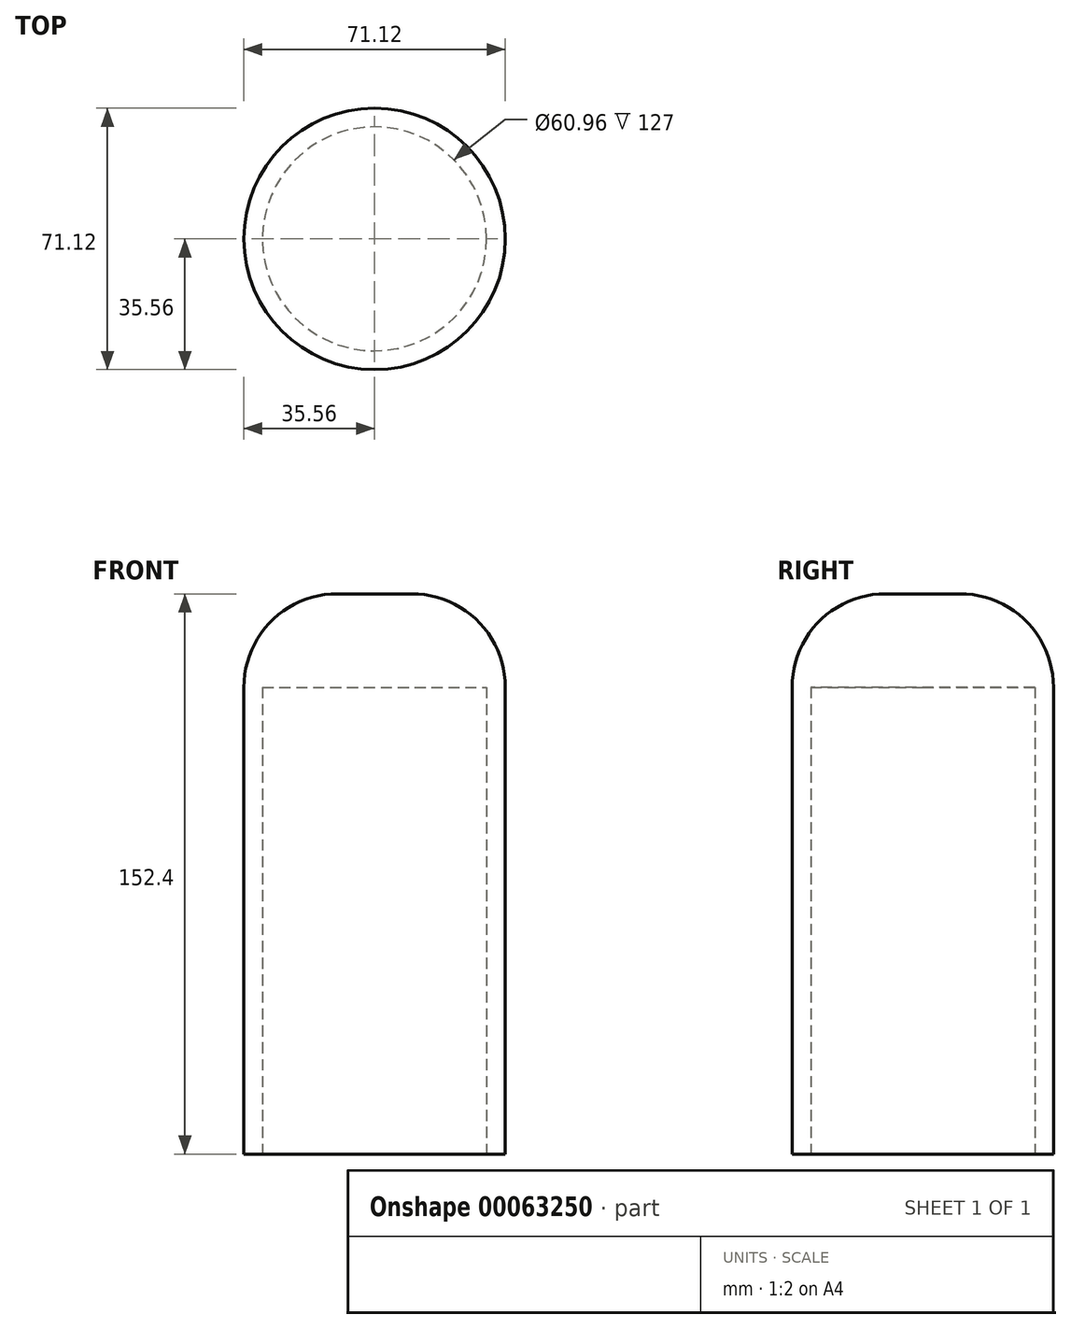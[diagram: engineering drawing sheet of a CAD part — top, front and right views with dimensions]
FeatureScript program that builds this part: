
annotation { "Feature Type Name" : "Feature", "Feature Type Description" : "" }
export const myFeature = defineFeature(function(context is Context, id is Id, definition is map)
    precondition{}
    {
        {
            var Q0;
            Q0=qCreatedBy(makeId("Top.planeOp"),FACE);
            var sketch = newSketch(context, id + "F0", { "sketchPlane" : qUnion([Q0])});
            skCircle(sketch, "E0", {"center": v(0, 0) * mm, "radius": 35.56 * mm});
            skSolve(sketch);
        }
        {
            var Q0;
            Q0=makeQuery(id+"F0.imprint","IMPRINT",FACE,{"disambiguationData":[TD([[makeQuery(id+"F0.imprint","IMPRINT",EDGE,{"derivedFrom":sQuery(id+"F0.wireOp",EDGE,"E0")}),1.0]])]});
            extrude(context, id + "F1", {"entities" : qUnion([Q0]), "depth" : 127 * mm});
        }
        {
            var Q0;
            Q0=makeQuery(id+"F1.opExtrude","CAP_FACE",FACE,{"disambiguationData":[OSD([sQuery(id+"F0.wireOp",EDGE,"E0")])],"isStart":false});
            extrude(context, id + "F2", {"entities" : qUnion([Q0]), "operationType" : NewBodyOperationType.ADD, "depth" : 25.4 * mm});
        }
        {
            var Q0;
            Q0=makeQuery(id+"F2.opExtrude","CAP_EDGE",EDGE,{"disambiguationData":[OSD([sQuery(id+"F0.wireOp",EDGE,"E0")])],"isStart":false});
            fillet(context, id + "F3", {"entities" : qUnion([Q0]), "radius" : 25.4 * mm, "tangentPropagation" : true, "allowEdgeOverflow" : false});
        }
        {
            var Q0;
            Q0=makeQuery(id+"F1.opExtrude","CAP_FACE",FACE,{"disambiguationData":[OSD([sQuery(id+"F0.wireOp",EDGE,"E0")])],"isStart":true});
            var sketch = newSketch(context, id + "F4", { "sketchPlane" : qUnion([Q0])});
            skCircle(sketch, "E1", {"center": v(0, 0) * mm, "radius": 30.48 * mm});
            skSolve(sketch);
        }
        {
            var Q0;
            Q0=makeQuery(id+"F4.imprint","IMPRINT",FACE,{"disambiguationData":[TD([[makeQuery(id+"F4.imprint","IMPRINT",EDGE,{"derivedFrom":sQuery(id+"F4.wireOp",EDGE,"E1")}),1.0]])]});
            extrude(context, id + "F5", {"entities" : qUnion([Q0]), "operationType" : NewBodyOperationType.REMOVE, "oppositeDirection" : true, "depth" : 127 * mm});
        }
    });
